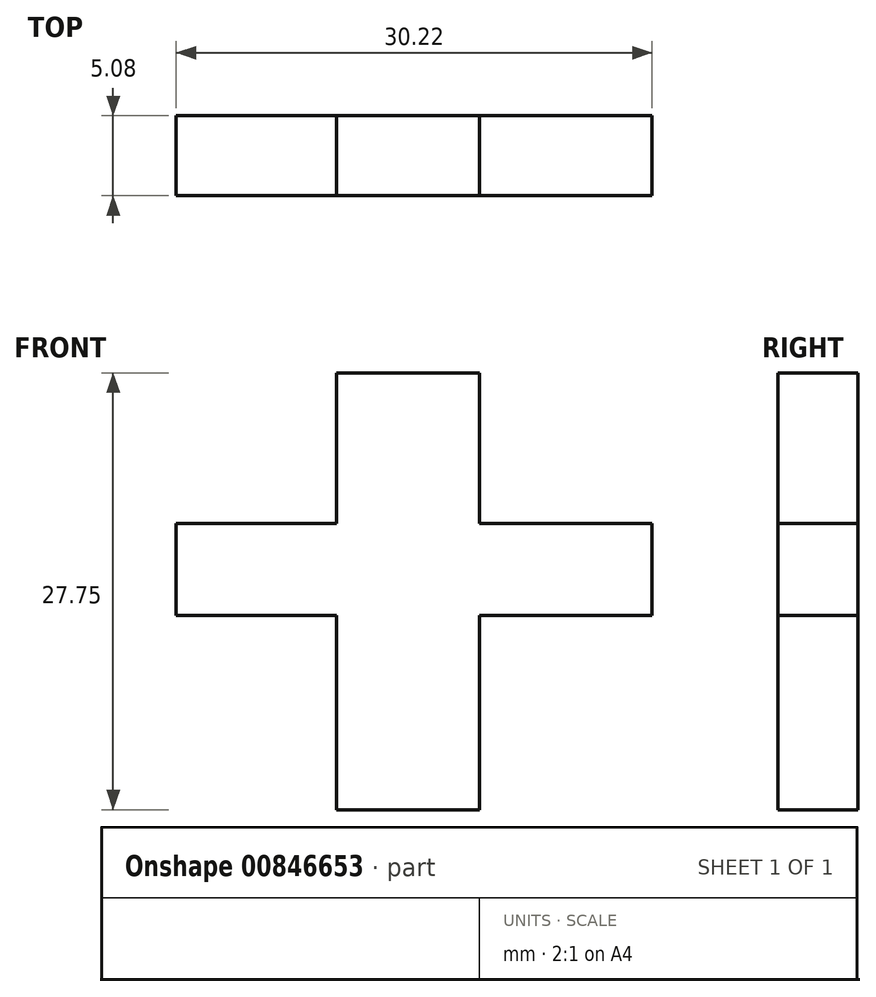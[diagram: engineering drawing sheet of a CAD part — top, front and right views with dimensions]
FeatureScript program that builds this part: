
annotation { "Feature Type Name" : "Feature", "Feature Type Description" : "" }
export const myFeature = defineFeature(function(context is Context, id is Id, definition is map)
    precondition{}
    {
        {
            var Q0;
            Q0=qCreatedBy(makeId("Front.planeOp"),FACE);
            var sketch = newSketch(context, id + "F0", { "sketchPlane" : qUnion([Q0])});
            skLineSegment(sketch, "E0", {"start": v(-9.1, 0) * mm, "end": v(-9.1, 27.75) * mm});
            skLineSegment(sketch, "E1", {"start": v(0, 0) * mm, "end": v(0, 27.75) * mm});
            skLineSegment(sketch, "E2", {"start": v(-9.1, 27.75) * mm, "end": v(0, 27.75) * mm});
            skLineSegment(sketch, "E3", {"start": v(-9.1, 0) * mm, "end": v(0, 0) * mm});
            skLineSegment(sketch, "E4", {"start": v(0, 18.2) * mm, "end": v(10.95, 18.2) * mm});
            skLineSegment(sketch, "E5", {"start": v(10.95, 18.2) * mm, "end": v(10.95, 12.33) * mm});
            skLineSegment(sketch, "E6", {"start": v(10.95, 12.33) * mm, "end": v(0, 12.33) * mm});
            skLineSegment(sketch, "E7", {"start": v(0, 12.33) * mm, "end": v(-9.1, 12.33) * mm});
            skLineSegment(sketch, "E8", {"start": v(-9.1, 12.33) * mm, "end": v(-19.27, 12.33) * mm});
            skLineSegment(sketch, "E9", {"start": v(-19.27, 12.33) * mm, "end": v(-19.27, 18.2) * mm});
            skLineSegment(sketch, "E10", {"start": v(-9.1, 18.2) * mm, "end": v(0, 18.2) * mm});
            skLineSegment(sketch, "E11", {"start": v(-9.1, 18.2) * mm, "end": v(-19.27, 18.2) * mm});
            skSolve(sketch);
        }
        {
            var Q0;
            {var subQ0=sQuery(id+"F0.wireOp",EDGE,"E2");Q0=makeQuery(id+"F0.imprint","IMPRINT",FACE,{"disambiguationData":[TD([[makeQuery(id+"F0.imprint","IMPRINT",EDGE,{"derivedFrom":subQ0}),-1.0]])]});}
            var Q1;
            {var subQ0=sQuery(id+"F0.wireOp",EDGE,"E7");Q1=makeQuery(id+"F0.imprint","IMPRINT",FACE,{"disambiguationData":[TD([[makeQuery(id+"F0.imprint","IMPRINT",EDGE,{"derivedFrom":subQ0}),-1.0]])]});}
            var Q2;
            {var subQ0=sQuery(id+"F0.wireOp",EDGE,"E8");Q2=makeQuery(id+"F0.imprint","IMPRINT",FACE,{"disambiguationData":[TD([[makeQuery(id+"F0.imprint","IMPRINT",EDGE,{"derivedFrom":subQ0}),-1.0]])]});}
            var Q3;
            {var subQ0=sQuery(id+"F0.wireOp",EDGE,"E4");Q3=makeQuery(id+"F0.imprint","IMPRINT",FACE,{"disambiguationData":[TD([[makeQuery(id+"F0.imprint","IMPRINT",EDGE,{"derivedFrom":subQ0}),-1.0]])]});}
            var Q4;
            {var subQ0=sQuery(id+"F0.wireOp",EDGE,"E3");Q4=makeQuery(id+"F0.imprint","IMPRINT",FACE,{"disambiguationData":[TD([[makeQuery(id+"F0.imprint","IMPRINT",EDGE,{"derivedFrom":subQ0}),1.0]])]});}
            extrude(context, id + "F1", {"entities" : qUnion([Q0, Q1, Q2, Q3, Q4]), "depth" : 5.08 * mm, "offsetDistance" : 25.4 * mm});
        }
    });
